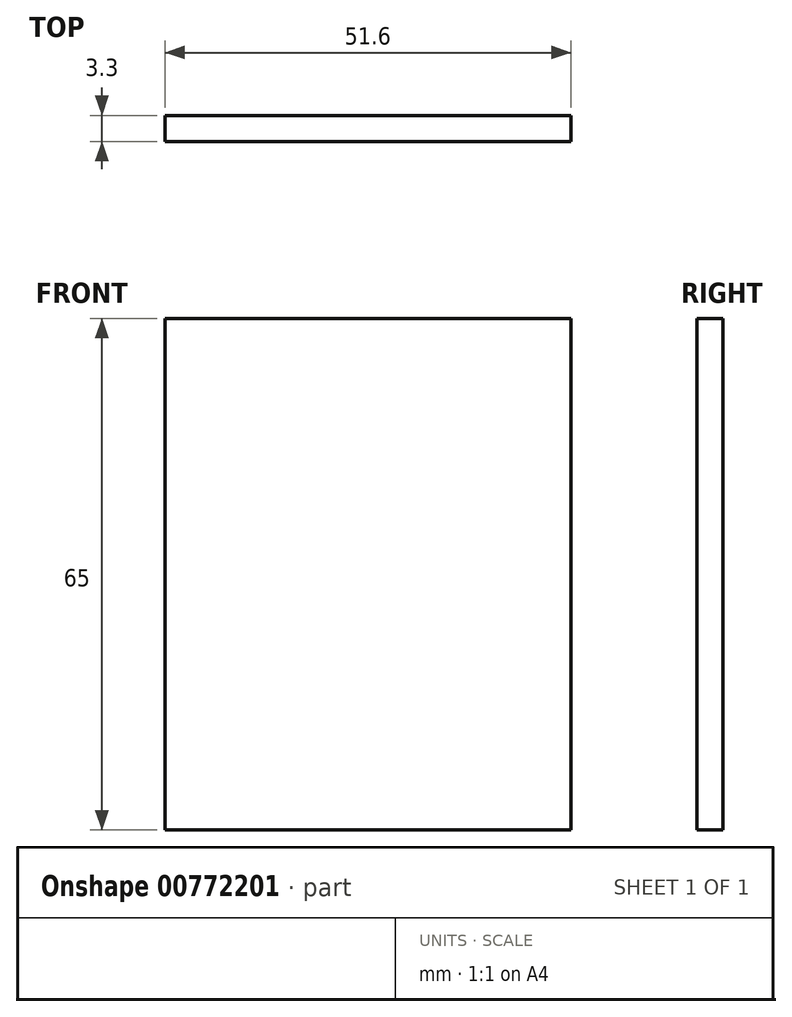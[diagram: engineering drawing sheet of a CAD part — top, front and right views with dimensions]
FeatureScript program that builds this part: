
annotation { "Feature Type Name" : "Feature", "Feature Type Description" : "" }
export const myFeature = defineFeature(function(context is Context, id is Id, definition is map)
    precondition{}
    {
        {
            var Q0;
            Q0=qCreatedBy(makeId("Front.planeOp"),FACE);
            var sketch = newSketch(context, id + "F0", { "sketchPlane" : qUnion([Q0])});
            skLineSegment(sketch, "E0.bottom", {"start": v(-36.54, 9.85) * mm, "end": v(15.06, 9.85) * mm});
            skLineSegment(sketch, "E0.top", {"start": v(-36.54, -55.15) * mm, "end": v(15.06, -55.15) * mm});
            skLineSegment(sketch, "E0.left", {"start": v(-36.54, 9.85) * mm, "end": v(-36.54, -55.15) * mm});
            skLineSegment(sketch, "E0.right", {"start": v(15.06, 9.85) * mm, "end": v(15.06, -55.15) * mm});
            skSolve(sketch);
        }
        {
            var Q0;
            Q0=makeQuery(id+"F0.imprint","IMPRINT",FACE,{"disambiguationData":[TD([[makeQuery(id+"F0.imprint","IMPRINT",EDGE,{"derivedFrom":sQuery(id+"F0.wireOp",EDGE,"E0.bottom")}),-1.0]])]});
            extrude(context, id + "F1", {"entities" : qUnion([Q0]), "depth" : 3.3 * mm, "offsetDistance" : 25 * mm});
        }
    });
